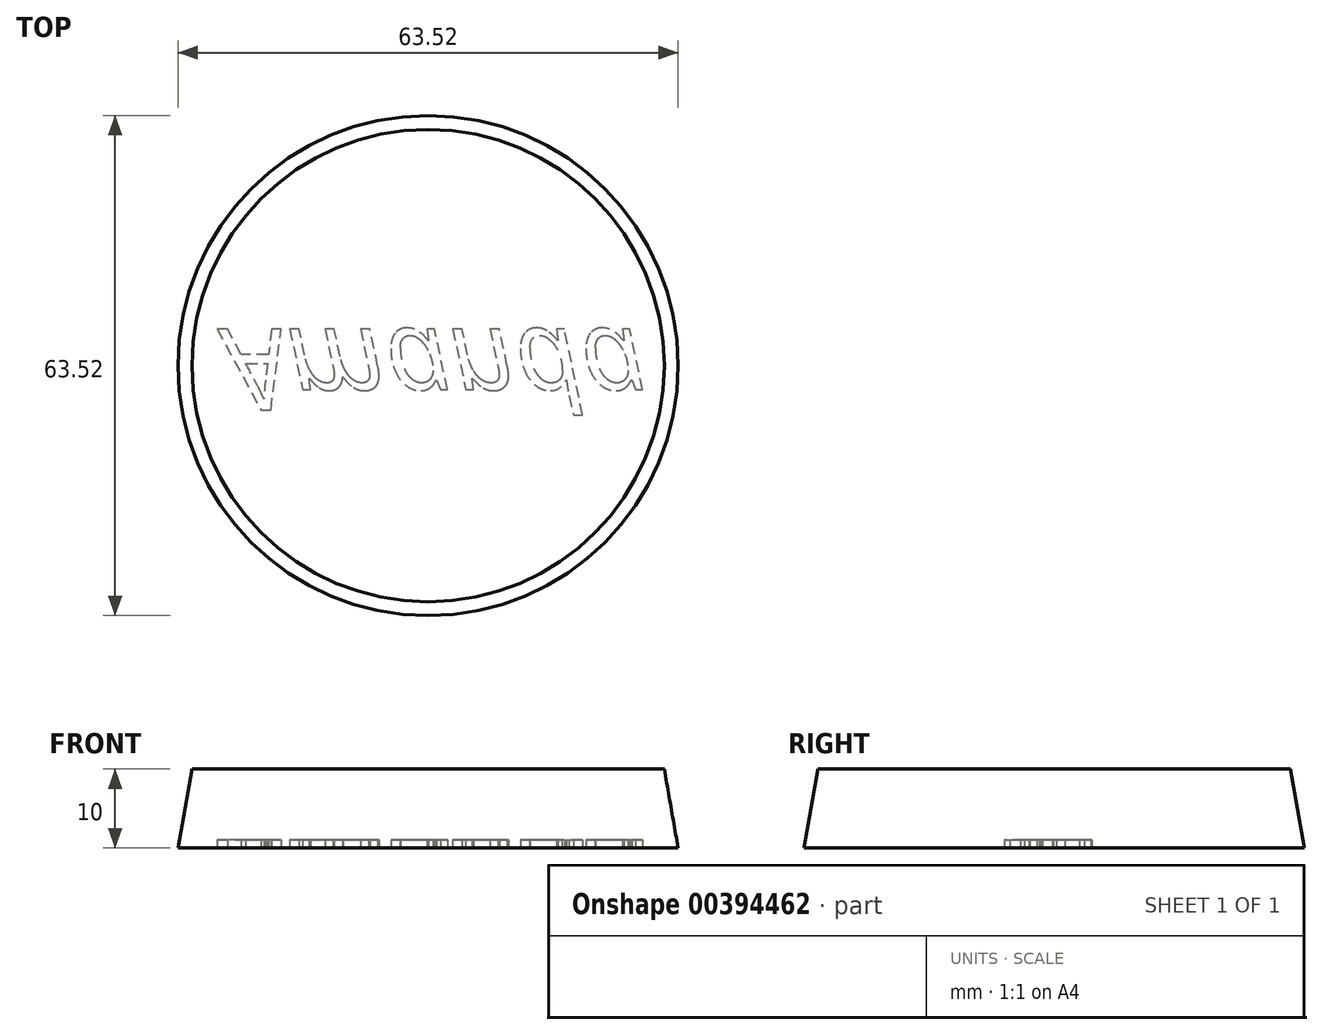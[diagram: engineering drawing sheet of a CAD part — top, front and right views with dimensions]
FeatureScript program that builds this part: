
annotation { "Feature Type Name" : "Feature", "Feature Type Description" : "" }
export const myFeature = defineFeature(function(context is Context, id is Id, definition is map)
    precondition{}
    {
        {
            var Q0;
            Q0=qCreatedBy(makeId("Top.planeOp"),FACE);
            var sketch = newSketch(context, id + "F0", { "sketchPlane" : qUnion([Q0])});
            skCircle(sketch, "E0", {"center": v(0, 0) * mm, "radius": 30 * mm});
            skSolve(sketch);
        }
        {
            var Q0;
            Q0=makeQuery(id+"F0.imprint","IMPRINT",FACE,{"disambiguationData":[TD([[makeQuery(id+"F0.imprint","IMPRINT",EDGE,{"derivedFrom":sQuery(id+"F0.wireOp",EDGE,"E0")}),1.0]])]});
            extrude(context, id + "F1", {"entities" : qUnion([Q0]), "oppositeDirection" : true, "depth" : 10 * mm, "hasDraft" : true, "draftAngle" : 10 * degree});
        }
        {
            var Q0;
            Q0=makeQuery(id+"F1.opExtrude","CAP_FACE",FACE,{"disambiguationData":[OSD([sQuery(id+"F0.wireOp",EDGE,"E0")])],"isStart":false});
            var sketch = newSketch(context, id + "F2", { "sketchPlane" : qUnion([Q0])});
            skText(sketch, "E1", { "text": "Amanda", "fontName": "OpenSans-Italic.ttf"});
            const initialGuessF2  = {"E1": [-0.026, -0.00467, 1, 0, 0.01038]};
            skSetInitialGuess(sketch, initialGuessF2);
            skSolve(sketch);
        }
        {
            var Q0;
            Q0=qSketchRegion(id+"F2",true);
            extrude(context, id + "F3", {"entities" : qUnion([Q0]), "operationType" : NewBodyOperationType.REMOVE, "oppositeDirection" : true, "depth" : 1 * mm});
        }
    });
